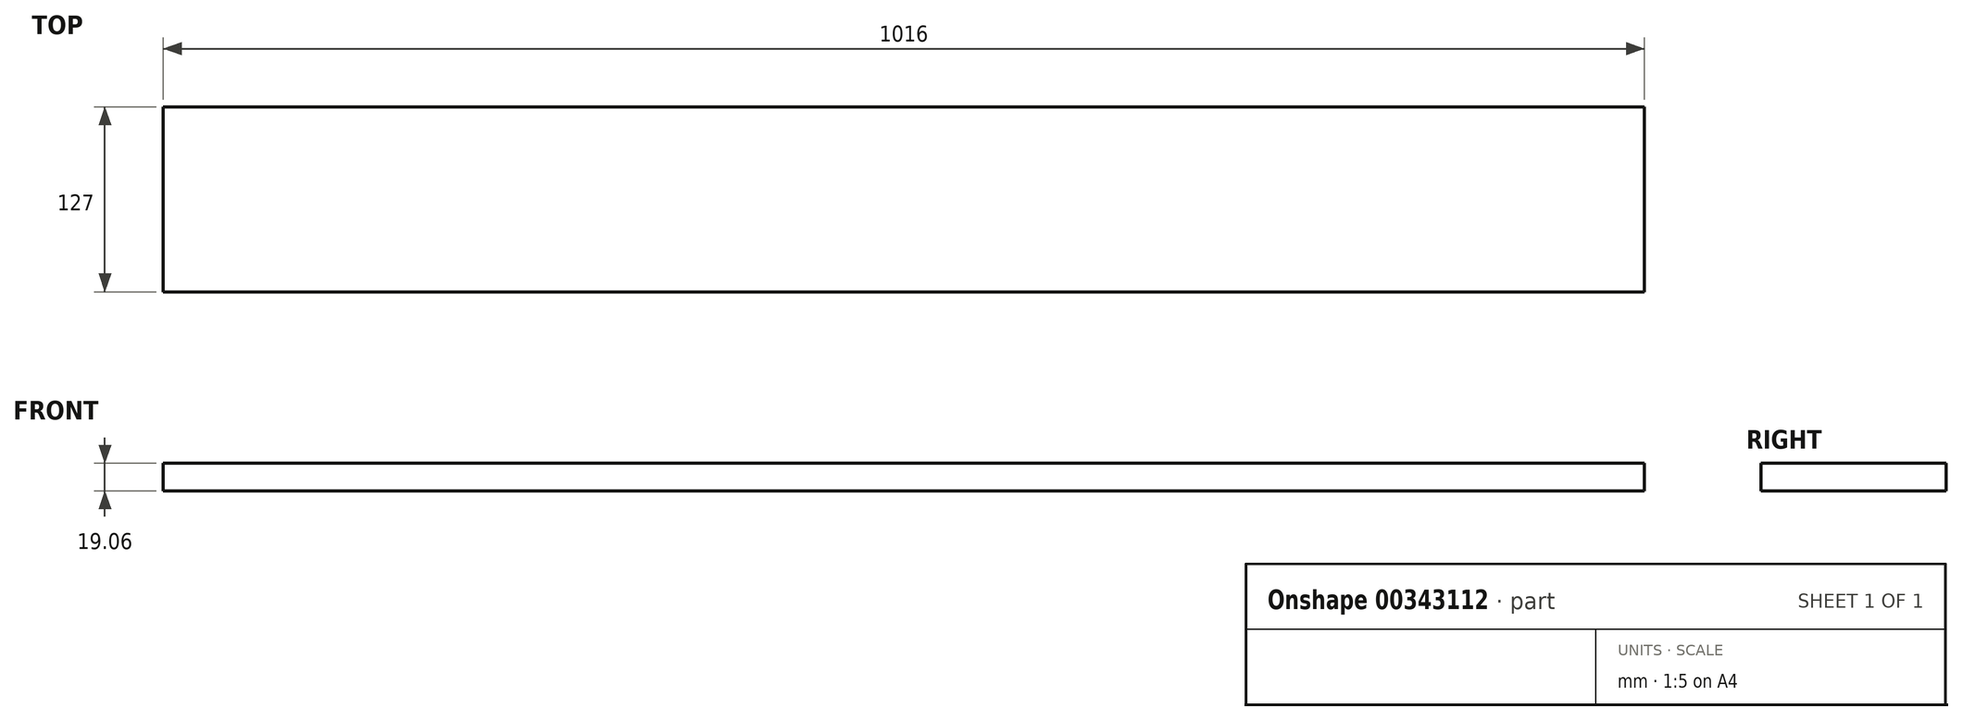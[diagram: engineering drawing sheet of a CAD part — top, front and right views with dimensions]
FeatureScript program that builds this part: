
annotation { "Feature Type Name" : "Feature", "Feature Type Description" : "" }
export const myFeature = defineFeature(function(context is Context, id is Id, definition is map)
    precondition{}
    {
        {
            var Q0;
            Q0=qCreatedBy(makeId("Right.planeOp"),FACE);
            var sketch = newSketch(context, id + "F0", { "sketchPlane" : qUnion([Q0])});
            skLineSegment(sketch, "E0.bottom", {"start": v(-63.5, 9.53) * mm, "end": v(63.5, 9.53) * mm});
            skLineSegment(sketch, "E0.top", {"start": v(-63.5, -9.52) * mm, "end": v(63.5, -9.52) * mm});
            skLineSegment(sketch, "E0.left", {"start": v(-63.5, 9.53) * mm, "end": v(-63.5, -9.52) * mm});
            skLineSegment(sketch, "E0.right", {"start": v(63.5, 9.53) * mm, "end": v(63.5, -9.52) * mm});
            skSolve(sketch);
        }
        {
            var Q0;
            Q0=makeQuery(id+"F0.imprint","IMPRINT",FACE,{"disambiguationData":[TD([[makeQuery(id+"F0.imprint","IMPRINT",EDGE,{"derivedFrom":sQuery(id+"F0.wireOp",EDGE,"E0.bottom")}),-1.0]])]});
            extrude(context, id + "F1", {"entities" : qUnion([Q0]), "endBound" : BoundingType.SYMMETRIC, "depth" : 1016 * mm});
        }
    });
